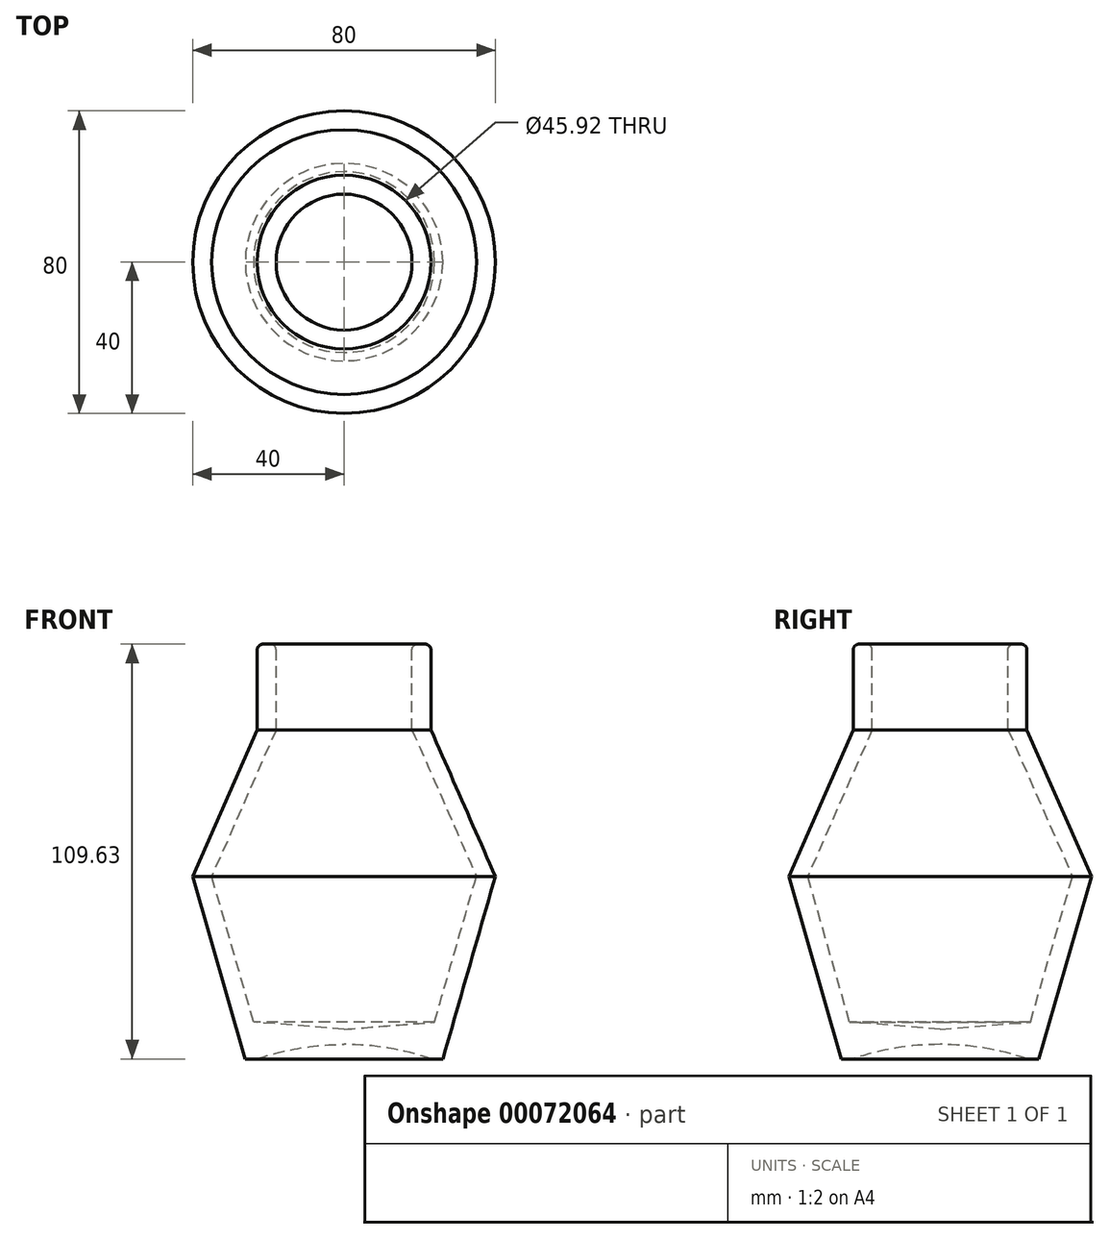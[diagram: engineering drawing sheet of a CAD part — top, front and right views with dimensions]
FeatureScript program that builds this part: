
annotation { "Feature Type Name" : "Feature", "Feature Type Description" : "" }
export const myFeature = defineFeature(function(context is Context, id is Id, definition is map)
    precondition{}
    {
        {
            var Q0;
            Q0=qCreatedBy(makeId("Front.planeOp"),FACE);
            var sketch = newSketch(context, id + "F0", { "sketchPlane" : qUnion([Q0])});
            skLineSegment(sketch, "E0", {"start": v(40, 0) * mm, "end": v(22.96, 38.77) * mm});
            skLineSegment(sketch, "E1", {"start": v(22.96, 38.77) * mm, "end": v(22.96, 61.4) * mm});
            skLineSegment(sketch, "E2", {"start": v(40, 0) * mm, "end": v(26.1, -48.24) * mm});
            skLineSegment(sketch, "E3", {"start": v(0, -44.41) * mm, "end": v(0, 47.06) * mm, "construction": true});
            skLineSegment(sketch, "E4", {"start": v(22.96, 61.4) * mm, "end": v(17.96, 61.4) * mm});
            skLineSegment(sketch, "E5", {"start": v(17.96, 61.4) * mm, "end": v(17.96, 38.77) * mm});
            skLineSegment(sketch, "E6", {"start": v(17.96, 38.77) * mm, "end": v(35, 0) * mm});
            skLineSegment(sketch, "E7", {"start": v(35, 0) * mm, "end": v(23.91, -38.5) * mm});
            skLineSegment(sketch, "E8", {"start": v(23.91, -38.5) * mm, "end": v(0, -40.41) * mm});
            skLineSegment(sketch, "E9", {"start": v(26.1, -48.24) * mm, "end": v(23.1, -48.24) * mm});
            skArc(sketch, "E10", {"start": v(23.1, -48.24) * mm, "mid": v(11.71, -45.38) * mm, "end": v(0, -44.41) * mm});
            skSolve(sketch);
        }
        {
            var Q0;
            Q0 = qConstructionFilter(qBodyType(qCreatedBy(id + "F0" ,EDGE), BodyType.WIRE), ConstructionObject.NO);
            var Q1;
            Q1=sQuery(id+"F0.wireOp",EDGE,"E3");
            revolve(context, id + "F1", {"bodyType" : ToolBodyType.SURFACE, "surfaceEntities" : qUnion([Q0]), "axis" : qUnion([Q1]), "revolveType" : RevolveType.FULL});
        }
        {
            var Q0;
            Q0=makeQuery(id+"F1.opRevolve","SWEPT_EDGE",EDGE,{"disambiguationData":[OSD([sQuery(id+"F0.wireOp",VERTEX,"E4.start")])]});
            var Q1;
            Q1=makeQuery(id+"F1.opRevolve","SWEPT_EDGE",EDGE,{"disambiguationData":[OSD([sQuery(id+"F0.wireOp",VERTEX,"E5.start")])]});
            fillet(context, id + "F2", {"entities" : qUnion([Q0, Q1]), "radius" : 1.5 * mm, "tangentPropagation" : true, "allowEdgeOverflow" : false});
        }
    });
